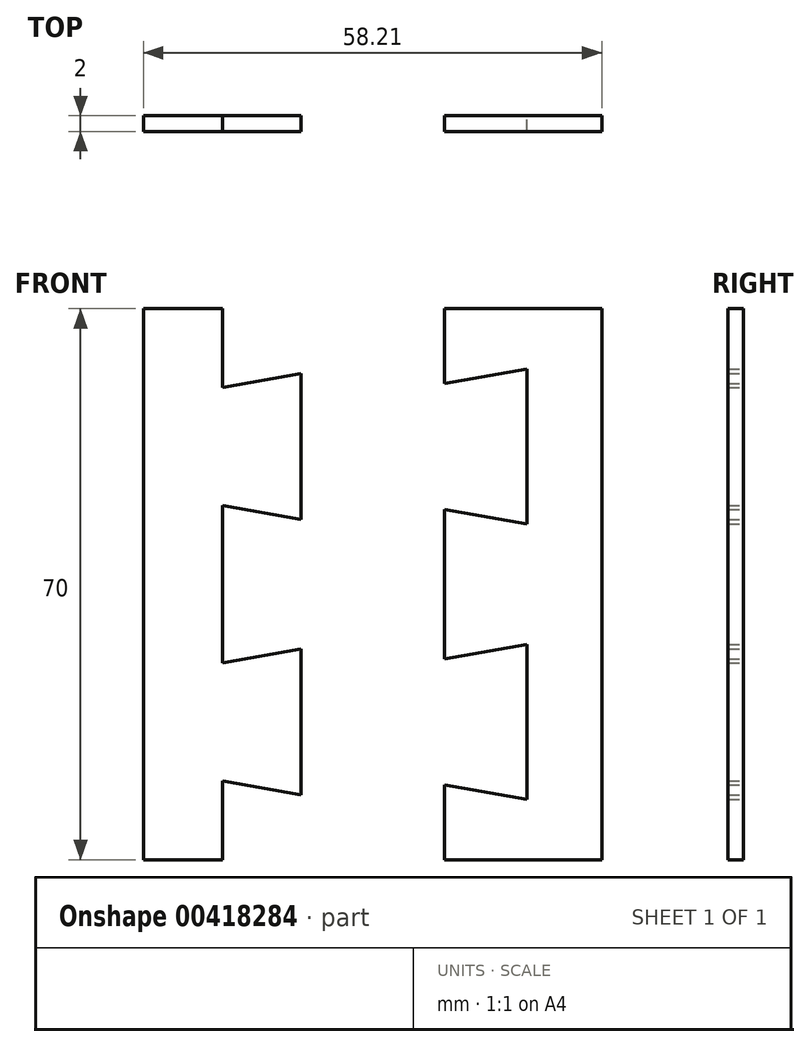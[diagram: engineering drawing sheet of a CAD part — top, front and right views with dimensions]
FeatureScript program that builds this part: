
annotation { "Feature Type Name" : "Feature", "Feature Type Description" : "" }
export const myFeature = defineFeature(function(context is Context, id is Id, definition is map)
    precondition{}
    {
        {
            var Q0;
            Q0=qCreatedBy(makeId("Front.planeOp"),FACE);
            var sketch = newSketch(context, id + "F0", { "sketchPlane" : qUnion([Q0])});
            skLineSegment(sketch, "E0", {"start": v(-63.33, 35) * mm, "end": v(-22.85, 35) * mm, "construction": true});
            skLineSegment(sketch, "E1", {"start": v(-12.85, 0) * mm, "end": v(-12.85, 10) * mm});
            skLineSegment(sketch, "E2", {"start": v(-12.85, 10) * mm, "end": v(-2.85, 8.24) * mm});
            skLineSegment(sketch, "E3", {"start": v(-2.85, 8.24) * mm, "end": v(-2.85, 26.76) * mm});
            skLineSegment(sketch, "E4", {"start": v(-2.85, 26.76) * mm, "end": v(-12.85, 25) * mm});
            skLineSegment(sketch, "E5", {"start": v(-12.85, 25) * mm, "end": v(-12.85, 35) * mm});
            skLineSegment(sketch, "E6", {"start": v(-12.85, 25) * mm, "end": v(-12.85, 10) * mm, "construction": true});
            skLineSegment(sketch, "E7", {"start": v(15.36, 0) * mm, "end": v(15.36, 9.5) * mm});
            skLineSegment(sketch, "E8", {"start": v(15.36, 9.5) * mm, "end": v(25.86, 7.65) * mm});
            skLineSegment(sketch, "E9", {"start": v(25.86, 7.65) * mm, "end": v(25.86, 27.35) * mm});
            skLineSegment(sketch, "E10", {"start": v(25.86, 27.35) * mm, "end": v(15.36, 25.5) * mm});
            skLineSegment(sketch, "E11", {"start": v(15.36, 25.5) * mm, "end": v(15.36, 35) * mm});
            skLineSegment(sketch, "E12", {"start": v(15.36, 25.5) * mm, "end": v(15.36, 9.5) * mm, "construction": true});
            skLineSegment(sketch, "E13", {"start": v(-22.85, 35) * mm, "end": v(-22.85, 0) * mm});
            skLineSegment(sketch, "E14", {"start": v(-22.85, 0) * mm, "end": v(-12.85, 0) * mm});
            skLineSegment(sketch, "E15", {"start": v(35.36, 35) * mm, "end": v(35.36, 0) * mm});
            skLineSegment(sketch, "E16", {"start": v(35.36, 0) * mm, "end": v(15.36, 0) * mm});
            skLineSegment(sketch, "E17.MirrorCS", {"start": v(35.36, 35) * mm, "end": v(35.36, 70) * mm});
            skLineSegment(sketch, "E18.MirrorCS", {"start": v(35.36, 70) * mm, "end": v(15.36, 70) * mm});
            skLineSegment(sketch, "E19.MirrorCS", {"start": v(15.36, 70) * mm, "end": v(15.36, 60.5) * mm});
            skLineSegment(sketch, "E20.MirrorCS", {"start": v(15.36, 60.5) * mm, "end": v(25.86, 62.35) * mm});
            skLineSegment(sketch, "E21.MirrorCS", {"start": v(25.86, 62.35) * mm, "end": v(25.86, 42.65) * mm});
            skLineSegment(sketch, "E22.MirrorCS", {"start": v(25.86, 42.65) * mm, "end": v(15.36, 44.5) * mm});
            skLineSegment(sketch, "E23.MirrorCS", {"start": v(15.36, 44.5) * mm, "end": v(15.36, 35) * mm});
            skLineSegment(sketch, "E24.MirrorCS", {"start": v(-12.85, 45) * mm, "end": v(-12.85, 35) * mm});
            skLineSegment(sketch, "E25.MirrorCS", {"start": v(-2.85, 43.24) * mm, "end": v(-12.85, 45) * mm});
            skLineSegment(sketch, "E26.MirrorCS", {"start": v(-2.85, 61.76) * mm, "end": v(-2.85, 43.24) * mm});
            skLineSegment(sketch, "E27.MirrorCS", {"start": v(-12.85, 60) * mm, "end": v(-2.85, 61.76) * mm});
            skLineSegment(sketch, "E28.MirrorCS", {"start": v(-12.85, 70) * mm, "end": v(-12.85, 60) * mm});
            skLineSegment(sketch, "E29.MirrorCS", {"start": v(-22.85, 70) * mm, "end": v(-12.85, 70) * mm});
            skLineSegment(sketch, "E30.MirrorCS", {"start": v(-22.85, 35) * mm, "end": v(-22.85, 70) * mm});
            skLineSegment(sketch, "E31.trimOffspring", {"start": v(-12.85, 35) * mm, "end": v(15.36, 35) * mm, "construction": true});
            skLineSegment(sketch, "E32.trimOffspring", {"start": v(35.36, 35) * mm, "end": v(65.6, 35) * mm, "construction": true});
            skSolve(sketch);
        }
        {
            var Q0;
            Q0=makeQuery(id+"F0.imprint","IMPRINT",FACE,{"disambiguationData":[TD([[makeQuery(id+"F0.imprint","IMPRINT",EDGE,{"derivedFrom":sQuery(id+"F0.wireOp",EDGE,"E1")}),1.0]])]});
            var Q1;
            Q1=makeQuery(id+"F0.imprint","IMPRINT",FACE,{"disambiguationData":[TD([[makeQuery(id+"F0.imprint","IMPRINT",EDGE,{"derivedFrom":sQuery(id+"F0.wireOp",EDGE,"E7")}),-1.0]])]});
            extrude(context, id + "F1", {"entities" : qUnion([Q0, Q1]), "depth" : 2 * mm});
        }
    });
